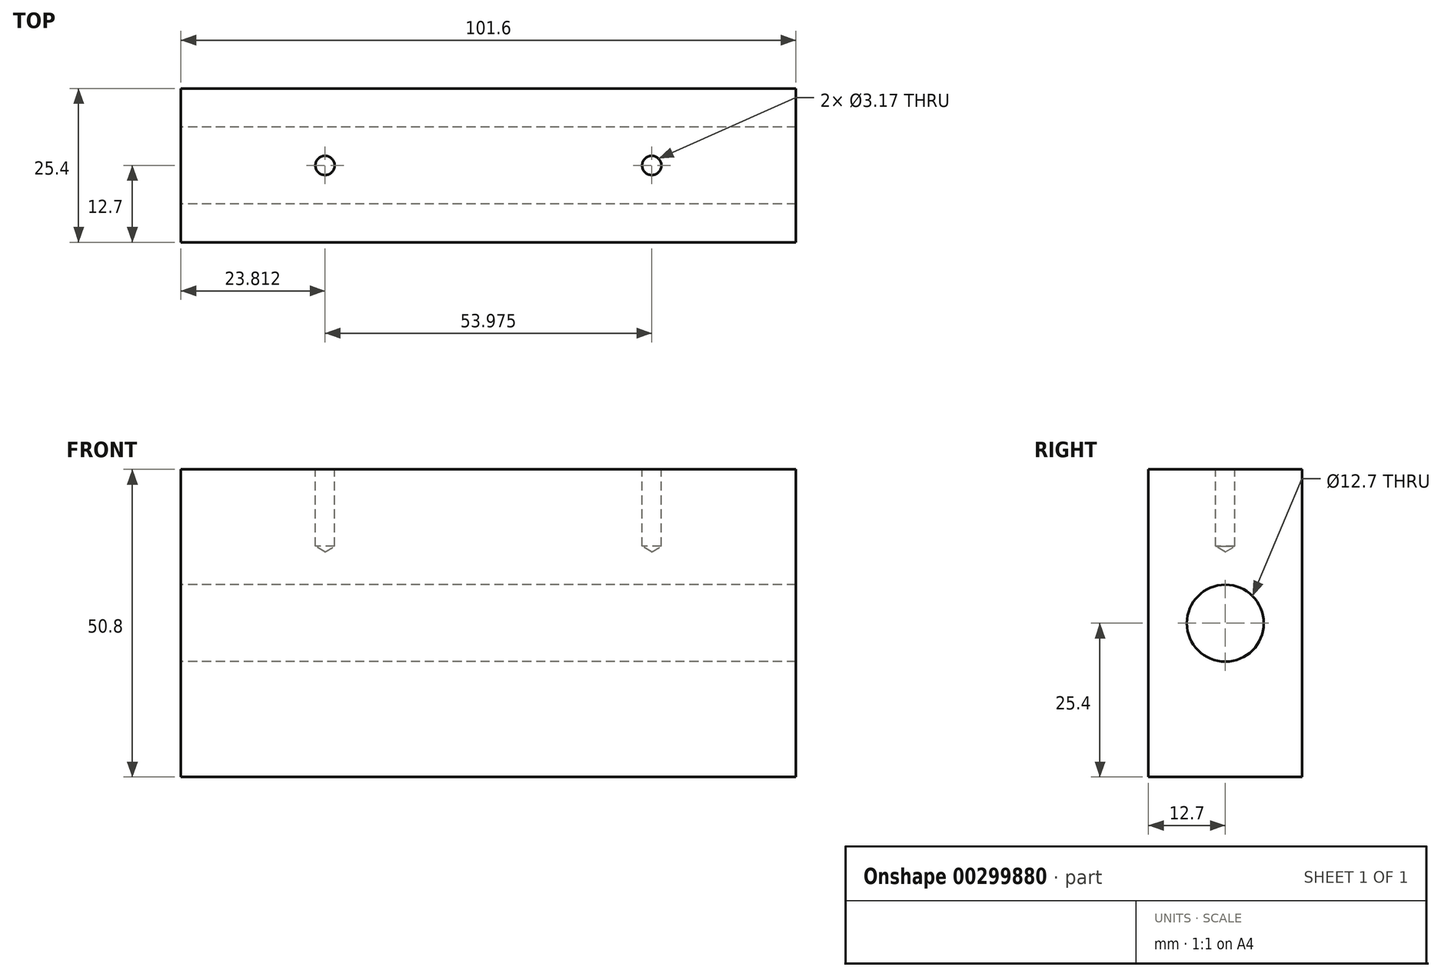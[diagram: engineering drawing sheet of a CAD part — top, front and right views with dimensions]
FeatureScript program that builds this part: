
annotation { "Feature Type Name" : "Feature", "Feature Type Description" : "" }
export const myFeature = defineFeature(function(context is Context, id is Id, definition is map)
    precondition{}
    {
        {
            var Q0;
            Q0=qCreatedBy(makeId("Top.planeOp"),FACE);
            var sketch = newSketch(context, id + "F0", { "sketchPlane" : qUnion([Q0])});
            skLineSegment(sketch, "E0.bottom", {"start": v(-50.8, 12.7) * mm, "end": v(50.8, 12.7) * mm});
            skLineSegment(sketch, "E0.top", {"start": v(-50.8, -12.7) * mm, "end": v(50.8, -12.7) * mm});
            skLineSegment(sketch, "E0.left", {"start": v(-50.8, 12.7) * mm, "end": v(-50.8, -12.7) * mm});
            skLineSegment(sketch, "E0.right", {"start": v(50.8, 12.7) * mm, "end": v(50.8, -12.7) * mm});
            skPoint(sketch, "E0.middle", {"position": v(0, 0) * mm});
            skSolve(sketch);
        }
        {
            var Q0;
            Q0=makeQuery(id+"F0.imprint","IMPRINT",FACE,{"disambiguationData":[TD([[makeQuery(id+"F0.imprint","IMPRINT",EDGE,{"derivedFrom":sQuery(id+"F0.wireOp",EDGE,"E0.bottom")}),-1.0]])]});
            extrude(context, id + "F1", {"entities" : qUnion([Q0]), "depth" : 50.8 * mm});
        }
        {
            var Q0;
            Q0=makeQuery(id+"F1.opExtrude","CAP_FACE",FACE,{"disambiguationData":[OSD([sQuery(id+"F0.wireOp",EDGE,"E0.bottom"),sQuery(id+"F0.wireOp",EDGE,"E0.top"),sQuery(id+"F0.wireOp",EDGE,"E0.left"),sQuery(id+"F0.wireOp",EDGE,"E0.right")])],"isStart":false});
            var sketch = newSketch(context, id + "F2", { "sketchPlane" : qUnion([Q0])});
            skCircle(sketch, "E1", {"center": v(-26.99, 0) * mm, "radius": 1.59 * mm});
            skCircle(sketch, "E2", {"center": v(26.99, 0) * mm, "radius": 1.59 * mm});
            skSolve(sketch);
        }
        {
            var Q0;
            Q0=sQuery(id+"F2.wireOp",VERTEX,"E1.center");
            var Q1;
            Q1=sQuery(id+"F2.wireOp",VERTEX,"E2.center");
            var Q2;
            Q2=makeQuery(id+"F1.opExtrude","SWEPT_BODY",BODY,{"disambiguationData":[OSD([sQuery(id+"F0.wireOp",EDGE,"E0.bottom"),sQuery(id+"F0.wireOp",EDGE,"E0.top"),sQuery(id+"F0.wireOp",EDGE,"E0.left"),sQuery(id+"F0.wireOp",EDGE,"E0.right")])]});
            hole(context, id + "F3", {"style" : HoleStyle.SIMPLE, "endStyle" : HoleEndStyle.BLIND, "holeDiameter" : 3.17 * mm, "holeDepth" : 12.7 * mm, "tappedDepth" : 12.7 * mm, "tapClearance" : 3, "locations" : qUnion([Q0, Q1]), "scope" : qUnion([Q2])});
        }
        {
            var Q0;
            Q0=makeQuery(id+"F1.opExtrude","SWEPT_FACE",FACE,{"disambiguationData":[OSD([sQuery(id+"F0.wireOp",EDGE,"E0.left")])]});
            var sketch = newSketch(context, id + "F4", { "sketchPlane" : qUnion([Q0])});
            skCircle(sketch, "E3", {"center": v(0, 25.4) * mm, "radius": 6.35 * mm});
            skSolve(sketch);
        }
        {
            var Q0;
            Q0=sQuery(id+"F4.wireOp",VERTEX,"E3.center");
            var Q1;
            Q1=makeQuery(id+"F1.opExtrude","SWEPT_BODY",BODY,{"disambiguationData":[OSD([sQuery(id+"F0.wireOp",EDGE,"E0.bottom"),sQuery(id+"F0.wireOp",EDGE,"E0.top"),sQuery(id+"F0.wireOp",EDGE,"E0.left"),sQuery(id+"F0.wireOp",EDGE,"E0.right")])]});
            hole(context, id + "F5", {"style" : HoleStyle.SIMPLE, "endStyle" : HoleEndStyle.THROUGH, "holeDiameter" : 12.7 * mm, "tappedDepth" : 12.7 * mm, "tapClearance" : 3, "locations" : qUnion([Q0]), "scope" : qUnion([Q1])});
        }
    });
